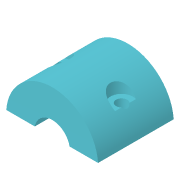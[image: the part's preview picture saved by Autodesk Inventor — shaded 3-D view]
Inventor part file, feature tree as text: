
AUTODESK INVENTOR PART (.ipt)
format: ipt  version: 2018 (Build 220112000, 112)  size: 135,168 bytes
history: native  units: in
note: dims shown in document units (in); Inventor stores cm internally (conversion verified against a paired STEP export)
features: extrude x3, sketch x3, plane x2, mirror x1
ambient origin geometry x8: Origin, YZ Plane, XZ Plane, XY Plane, X Axis, Y Axis, Z Axis, Center Point
bodies: Solid1 (feature_tree)
feature tree (9):
  extrude  "Extrusion1"  Depth=0.25in
  plane  "Work Plane2"
  extrude  "Extrusion2"  Depth=0.0234in
  extrude  "Extrusion3"  [1 undecoded]
  mirror  "Mirror1"
  sketch  "Sketch1"  dims[d0=0.65in d1=0.25in]
  plane  "Work Plane1"
  sketch  "Sketch2"  dims[d2=0.0469in d3=0.0234in]
  sketch  "Sketch3"  dims[d4=0.5344in d5=0.0in d6=-0.325in d7=0.0787in d8=0.2014in d9=0.1007in d10=0.5344in d11=0.2672in d12=1.0in d13=0.0in d14=0.1575in d15=0.1181in d16=0.0in]
note: 1 required parameter value undecoded (feature->parameter linkage not recoverable at this tier; creation-order binding heuristic only, values carry confidence <= 0.55)
